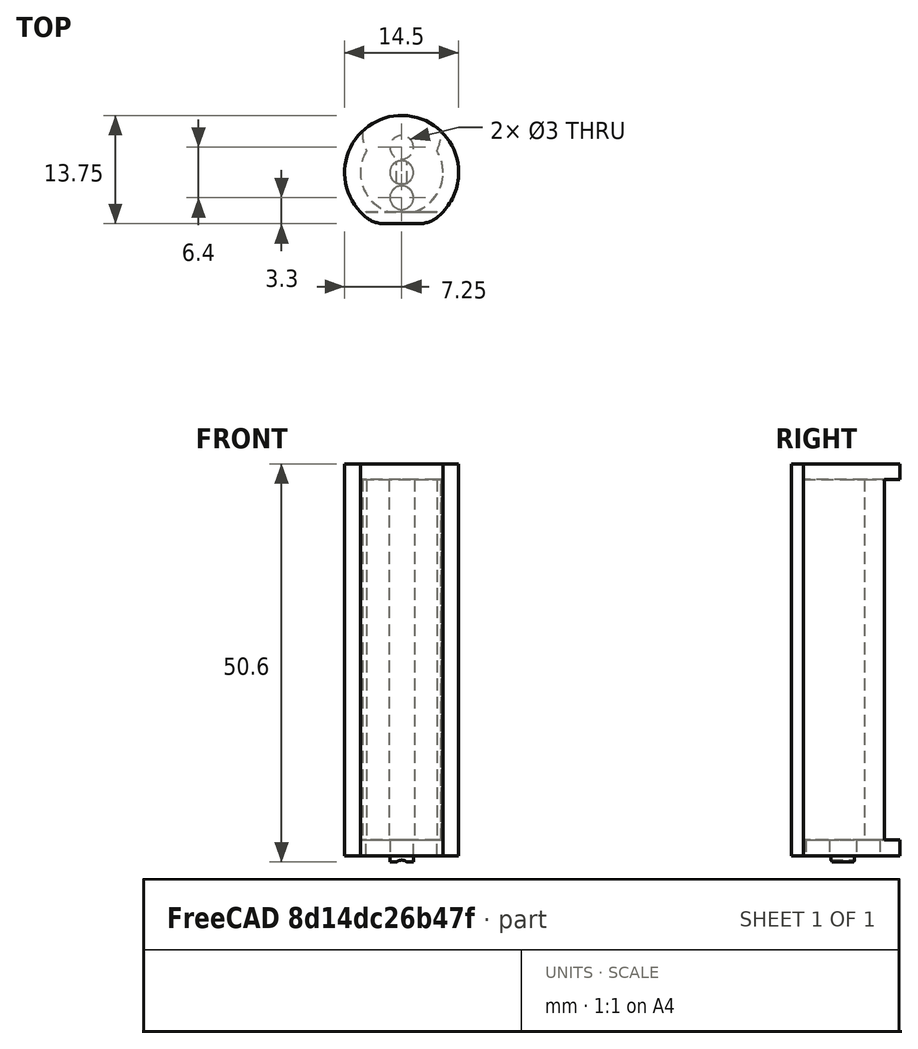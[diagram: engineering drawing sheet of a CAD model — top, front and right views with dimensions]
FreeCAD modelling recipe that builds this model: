
FCSTD DOCUMENT  (FreeCAD 0.21R33771 (Git))
Label: AABatteryJLW2406716
License: All rights reserved
LicenseURL: https://en.wikipedia.org/wiki/All_rights_reserved
objects: PartDesign::SubtractiveCylinder×5, PartDesign::SubtractiveBox×3, PartDesign::AdditiveBox×3, PartDesign::AdditiveCylinder×2, PartDesign::Chamfer×1, PartDesign::Fillet×1, PartDesign::Body×1
note: 31 computed .brp shape members not serialized (recipe doc carries the construction recipe); baked Part::Feature solids carry a one-line shape summary decoded from their .brp

FEATURE [PartDesign::AdditiveCylinder] Cylinder  label="Main body"
  Angle = 360
  AttacherType = Attacher::AttachEngine3D
  FirstAngle = 0
  Height = 49.8
  MapMode = 5
  Radius = 7.25
  SecondAngle = 0
  Support = -> [XY_Plane]
FEATURE [PartDesign::AdditiveCylinder] Cylinder003  label="End nub"
  Angle = 360
  AttacherType = Attacher::AttachEngine3D
  AttachmentOffset = pos=(0,0,-0.8) rot=(0,0,1;0rad)
  BaseFeature = -> Cylinder
  FirstAngle = 0
  Height = 1
  MapMode = 5
  Placement = pos=(0,0,-0.8) rot=(0,0,1;0rad)
  Radius = 1.5
  SecondAngle = 0
  Support = -> [XY_Plane]
FEATURE [PartDesign::SubtractiveCylinder] Cylinder001  label="Hollow out center"
  Angle = 360
  AttacherType = Attacher::AttachEngine3D
  AttachmentOffset = pos=(0,0,2) rot=(0,0,1;0rad)
  BaseFeature = -> Cylinder003
  FirstAngle = 0
  Height = 45.8
  MapMode = 5
  Placement = pos=(0,0,2) rot=(0,0,1;0rad)
  Radius = 5.25
  SecondAngle = 0
  Support = -> [XY_Plane]
FEATURE [PartDesign::SubtractiveCylinder] Cylinder002  label="Remove door on top"
  Angle = 360
  AttacherType = Attacher::AttachEngine3D
  AttachmentOffset = pos=(0,5,2) rot=(0,0,1;0rad)
  BaseFeature = -> Cylinder001
  FirstAngle = 0
  Height = 45.8
  MapMode = 5
  Placement = pos=(0,5,2) rot=(0,0,1;0rad)
  Radius = 5
  SecondAngle = 0
  Support = -> [XY_Plane]
FEATURE [PartDesign::SubtractiveBox] Box  label="xWid1p5 Slot for terminal head"
  AttacherType = Attacher::AttachEngine3D
  AttachmentOffset = pos=(-4.5,-5,0) rot=(0,0,1;0rad)
  BaseFeature = -> Cylinder002
  Height = 2
  Length = 9
  MapMode = 5
  Placement = pos=(-4.5,-5,0) rot=(0,0,1;0rad)
  Support = -> [XY_Plane]
  Width = 0.01
FEATURE [PartDesign::SubtractiveBox] Box006  label="x Yoffset -5 Open area for terminal head insertion"
  AttacherType = Attacher::AttachEngine3D
  AttachmentOffset = pos=(-4.5,-2,2) rot=(0,0,1;0rad)
  BaseFeature = -> Box
  Height = 8
  Length = 9
  MapMode = 5
  Placement = pos=(-4.5,-2,2) rot=(0,0,1;0rad)
  Support = -> [XY_Plane]
  Width = 3
FEATURE [PartDesign::SubtractiveBox] Box002  label="Cut off bottom of cylinder"
  AttacherType = Attacher::AttachEngine3D
  AttachmentOffset = pos=(-7.5,-15,0) rot=(0,0,1;0rad)
  BaseFeature = -> Box006
  Height = 49.8
  Length = 15
  MapMode = 5
  Placement = pos=(-7.5,-15,0) rot=(0,0,1;0rad)
  Support = -> [XY_Plane]
  Width = 10
FEATURE [PartDesign::AdditiveBox] Box003  label="Add flat bottom"
  AttacherType = Attacher::AttachEngine3D
  AttachmentOffset = pos=(-5.25,-6.5,0) rot=(0,0,1;0rad)
  BaseFeature = -> Box002
  Height = 49.8
  Length = 10.5
  MapMode = 5
  Placement = pos=(-5.25,-6.5,0) rot=(0,0,1;0rad)
  Support = -> [XY_Plane]
  Width = 1.5
FEATURE [PartDesign::Chamfer] Chamfer
  Angle = 45
  Base = -> Box003 [Edge13,Edge22]
  BaseFeature = -> Box003
  ChamferType = 0
  FlipDirection = false
  Placement = pos=(-5.25,-6.5,0) rot=(0,0,1;0rad)
  Size = 1.499
  Size2 = 1
  SupportTransform = false
  UseAllEdges = false
FEATURE [PartDesign::Fillet] Fillet
  Base = -> Chamfer [Edge11,Edge23]
  BaseFeature = -> Chamfer
  Placement = pos=(-5.25,-6.5,0) rot=(0,0,1;0rad)
  Radius = 3.75
  SupportTransform = false
  UseAllEdges = false
FEATURE [PartDesign::AdditiveBox] Box004  label="xWid 6 Narrow inside to hold crimp steady 1"
  AttacherType = Attacher::AttachEngine3D
  AttachmentOffset = pos=(-5,-5,10) rot=(0,0,1;0rad)
  BaseFeature = -> Fillet
  Height = 5
  Length = 2.75
  MapMode = 5
  Placement = pos=(-5,-5,10) rot=(0,0,1;0rad)
  Support = -> [XY_Plane]
  Width = 0.1
FEATURE [PartDesign::AdditiveBox] Box005  label="xWid 6 Narrow inside to hold crimp steady 2"
  AttacherType = Attacher::AttachEngine3D
  AttachmentOffset = pos=(2.25,-5,10) rot=(0,0,1;0rad)
  BaseFeature = -> Box004
  Height = 5
  Length = 2.75
  MapMode = 5
  Placement = pos=(2.25,-5,10) rot=(0,0,1;0rad)
  Support = -> [XY_Plane]
  Width = 0.1
FEATURE [PartDesign::SubtractiveCylinder] Cylinder004  label="Wire channel in end nub"
  Angle = 360
  AttacherType = Attacher::AttachEngine3D
  AttachmentOffset = pos=(0,-1.55,-2) rot=(0,0,1;0rad)
  BaseFeature = -> Box005
  FirstAngle = 0
  Height = 4
  MapMode = 5
  Placement = pos=(0,2,-1.55) rot=(1,0,0;1.5708rad)
  Radius = 1
  SecondAngle = 0
  Support = -> [XZ_Plane]
FEATURE [PartDesign::SubtractiveCylinder] Cylinder005  label="Bottom hole"
  Angle = 360
  AttacherType = Attacher::AttachEngine3D
  AttachmentOffset = pos=(0,-3.2,0) rot=(0,0,1;0rad)
  BaseFeature = -> Cylinder004
  FirstAngle = 0
  Height = 2
  MapMode = 5
  Placement = pos=(0,-3.2,0) rot=(0,0,1;0rad)
  Radius = 1.5
  SecondAngle = 0
  Support = -> [XY_Plane]
FEATURE [PartDesign::SubtractiveCylinder] Cylinder006  label="Top hole"
  Angle = 360
  AttacherType = Attacher::AttachEngine3D
  AttachmentOffset = pos=(0,3.2,0) rot=(0,0,1;0rad)
  BaseFeature = -> Cylinder005
  FirstAngle = 0
  Height = 2
  MapMode = 5
  Placement = pos=(0,3.2,0) rot=(0,0,1;0rad)
  Radius = 1.5
  SecondAngle = 0
  Support = -> [XY_Plane]
FEATURE [PartDesign::Body] Body  label="AABattery"
  Group = -> [Cylinder,Cylinder003,Cylinder001,Cylinder002,Box,Box006,Box002,Box003,Chamfer,Fillet,Box004,Box005,Cylinder004,Cylinder005,Cylinder006]
  Origin = -> Origin
  Tip = -> Cylinder006
